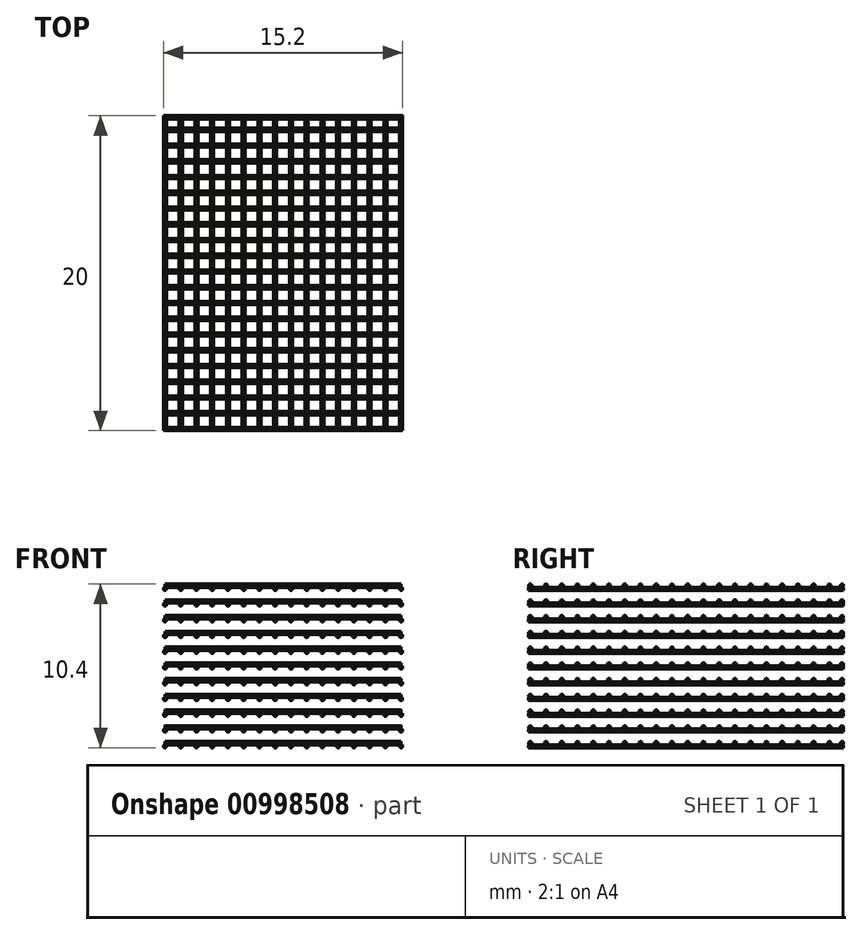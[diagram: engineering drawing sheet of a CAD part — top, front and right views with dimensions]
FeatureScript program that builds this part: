
annotation { "Feature Type Name" : "Feature", "Feature Type Description" : "" }
export const myFeature = defineFeature(function(context is Context, id is Id, definition is map)
    precondition{}
    {
        {
            var Q0;
            Q0=qCreatedBy(makeId("Front.planeOp"),FACE);
            var sketch = newSketch(context, id + "F0", { "sketchPlane" : qUnion([Q0])});
            skCircle(sketch, "E0", {"center": v(-15, 5) * mm, "radius": 0.1 * mm});
            skLineSegment(sketch, "E1.bottom", {"start": v(-15, 5) * mm, "end": v(0, 5) * mm, "construction": true});
            skLineSegment(sketch, "E1.top", {"start": v(-15, -5) * mm, "end": v(0, -5) * mm, "construction": true});
            skLineSegment(sketch, "E1.left", {"start": v(-15, 5) * mm, "end": v(-15, -5) * mm, "construction": true});
            skLineSegment(sketch, "E1.right", {"start": v(0, 5) * mm, "end": v(0, -5) * mm, "construction": true});
            skCircle(sketch, "E2", {"center": v(-15, -5) * mm, "radius": 0.1 * mm});
            skCircle(sketch, "E3", {"center": v(0, 5) * mm, "radius": 0.1 * mm});
            skCircle(sketch, "E4", {"center": v(0, -5) * mm, "radius": 0.1 * mm});
            skCircle(sketch, "E5", {"center": v(-15, 4) * mm, "radius": 0.1 * mm});
            skCircle(sketch, "E6", {"center": v(-15, 3) * mm, "radius": 0.1 * mm});
            skCircle(sketch, "E7", {"center": v(-15, 2) * mm, "radius": 0.1 * mm});
            skCircle(sketch, "E8", {"center": v(-15, 1) * mm, "radius": 0.1 * mm});
            skCircle(sketch, "E9", {"center": v(-15, 0) * mm, "radius": 0.1 * mm});
            skCircle(sketch, "E10", {"center": v(-15, -1) * mm, "radius": 0.1 * mm});
            skCircle(sketch, "E11", {"center": v(-15, -2) * mm, "radius": 0.1 * mm});
            skCircle(sketch, "E12", {"center": v(-15, -3) * mm, "radius": 0.1 * mm});
            skCircle(sketch, "E13", {"center": v(-15, -4) * mm, "radius": 0.1 * mm});
            skCircle(sketch, "E14", {"center": v(-10, 5) * mm, "radius": 0.1 * mm});
            skCircle(sketch, "E15", {"center": v(-9, 5) * mm, "radius": 0.1 * mm});
            skCircle(sketch, "E16", {"center": v(-8, 5) * mm, "radius": 0.1 * mm});
            skCircle(sketch, "E17", {"center": v(-7, 5) * mm, "radius": 0.1 * mm});
            skCircle(sketch, "E18", {"center": v(-6, 5) * mm, "radius": 0.1 * mm});
            skCircle(sketch, "E19", {"center": v(-5, 5) * mm, "radius": 0.1 * mm});
            skCircle(sketch, "E20", {"center": v(-4, 5) * mm, "radius": 0.1 * mm});
            skCircle(sketch, "E21", {"center": v(-3, 5) * mm, "radius": 0.1 * mm});
            skCircle(sketch, "E22", {"center": v(-2, 5) * mm, "radius": 0.1 * mm});
            skCircle(sketch, "E23", {"center": v(-1, 5) * mm, "radius": 0.1 * mm});
            skCircle(sketch, "E24", {"center": v(-13, 5) * mm, "radius": 0.1 * mm});
            skCircle(sketch, "E25", {"center": v(-12, 5) * mm, "radius": 0.1 * mm});
            skCircle(sketch, "E26", {"center": v(-11, 5) * mm, "radius": 0.1 * mm});
            skCircle(sketch, "E27", {"center": v(-14, 5) * mm, "radius": 0.1 * mm});
            skCircle(sketch, "E28", {"center": v(0, 4) * mm, "radius": 0.1 * mm});
            skCircle(sketch, "E29", {"center": v(0, 3) * mm, "radius": 0.1 * mm});
            skCircle(sketch, "E30", {"center": v(0, 2) * mm, "radius": 0.1 * mm});
            skCircle(sketch, "E31", {"center": v(0, -4) * mm, "radius": 0.1 * mm});
            skCircle(sketch, "E32", {"center": v(0, -3) * mm, "radius": 0.1 * mm});
            skCircle(sketch, "E33", {"center": v(0, 0) * mm, "radius": 0.1 * mm});
            skCircle(sketch, "E34", {"center": v(0, -2) * mm, "radius": 0.1 * mm});
            skCircle(sketch, "E35", {"center": v(0, -1) * mm, "radius": 0.1 * mm});
            skCircle(sketch, "E36", {"center": v(0, 1) * mm, "radius": 0.1 * mm});
            skCircle(sketch, "E37", {"center": v(-12, -5) * mm, "radius": 0.1 * mm});
            skCircle(sketch, "E38", {"center": v(-11, -5) * mm, "radius": 0.1 * mm});
            skCircle(sketch, "E39", {"center": v(-10, -5) * mm, "radius": 0.1 * mm});
            skCircle(sketch, "E40", {"center": v(-6, -5) * mm, "radius": 0.1 * mm});
            skCircle(sketch, "E41", {"center": v(-5, -5) * mm, "radius": 0.1 * mm});
            skCircle(sketch, "E42", {"center": v(-4, -5) * mm, "radius": 0.1 * mm});
            skCircle(sketch, "E43", {"center": v(-3, -5) * mm, "radius": 0.1 * mm});
            skCircle(sketch, "E44", {"center": v(-2, -5) * mm, "radius": 0.1 * mm});
            skCircle(sketch, "E45", {"center": v(-1, -5) * mm, "radius": 0.1 * mm});
            skCircle(sketch, "E46", {"center": v(-7, -5) * mm, "radius": 0.1 * mm});
            skCircle(sketch, "E47", {"center": v(-8, -5) * mm, "radius": 0.1 * mm});
            skCircle(sketch, "E48", {"center": v(-9, -5) * mm, "radius": 0.1 * mm});
            skCircle(sketch, "E49", {"center": v(-13, -5) * mm, "radius": 0.1 * mm});
            skCircle(sketch, "E50", {"center": v(-14, -5) * mm, "radius": 0.1 * mm});
            skLineSegment(sketch, "E51", {"start": v(-15, 4.5) * mm, "end": v(0, 4.5) * mm, "construction": true});
            skLineSegment(sketch, "E52", {"start": v(-15, 3.5) * mm, "end": v(0, 3.5) * mm, "construction": true});
            skLineSegment(sketch, "E53", {"start": v(-15, 2.5) * mm, "end": v(0, 2.5) * mm, "construction": true});
            skLineSegment(sketch, "E54", {"start": v(-15, 1.5) * mm, "end": v(0, 1.5) * mm, "construction": true});
            skCircle(sketch, "E55.MirrorC", {"center": v(-14, 4) * mm, "radius": 0.1 * mm});
            skLineSegment(sketch, "E56", {"start": v(-15, 0.5) * mm, "end": v(0, 0.5) * mm, "construction": true});
            skCircle(sketch, "E57.MirrorC", {"center": v(-13, 4) * mm, "radius": 0.1 * mm});
            skCircle(sketch, "E58.MirrorC", {"center": v(-12, 4) * mm, "radius": 0.1 * mm});
            skCircle(sketch, "E59.MirrorC", {"center": v(-11, 4) * mm, "radius": 0.1 * mm});
            skCircle(sketch, "E60.MirrorC", {"center": v(-10, 4) * mm, "radius": 0.1 * mm});
            skCircle(sketch, "E61.MirrorC", {"center": v(-9, 4) * mm, "radius": 0.1 * mm});
            skCircle(sketch, "E62.MirrorC", {"center": v(-8, 4) * mm, "radius": 0.1 * mm});
            skCircle(sketch, "E63.MirrorC", {"center": v(-7, 4) * mm, "radius": 0.1 * mm});
            skCircle(sketch, "E64.MirrorC", {"center": v(-6, 4) * mm, "radius": 0.1 * mm});
            skCircle(sketch, "E65.MirrorC", {"center": v(-5, 4) * mm, "radius": 0.1 * mm});
            skCircle(sketch, "E66.MirrorC", {"center": v(-4, 4) * mm, "radius": 0.1 * mm});
            skCircle(sketch, "E67.MirrorC", {"center": v(-3, 4) * mm, "radius": 0.1 * mm});
            skCircle(sketch, "E68.MirrorC", {"center": v(-2, 4) * mm, "radius": 0.1 * mm});
            skCircle(sketch, "E69.MirrorC", {"center": v(-1, 4) * mm, "radius": 0.1 * mm});
            skCircle(sketch, "E70.MirrorC", {"center": v(-1, 3) * mm, "radius": 0.1 * mm});
            skCircle(sketch, "E71.MirrorC", {"center": v(-2, 3) * mm, "radius": 0.1 * mm});
            skCircle(sketch, "E72.MirrorC", {"center": v(-3, 3) * mm, "radius": 0.1 * mm});
            skCircle(sketch, "E73.MirrorC", {"center": v(-4, 3) * mm, "radius": 0.1 * mm});
            skCircle(sketch, "E74.MirrorC", {"center": v(-5, 3) * mm, "radius": 0.1 * mm});
            skCircle(sketch, "E75.MirrorC", {"center": v(-6, 3) * mm, "radius": 0.1 * mm});
            skCircle(sketch, "E76.MirrorC", {"center": v(-7, 3) * mm, "radius": 0.1 * mm});
            skCircle(sketch, "E77.MirrorC", {"center": v(-8, 3) * mm, "radius": 0.1 * mm});
            skCircle(sketch, "E78.MirrorC", {"center": v(-9, 3) * mm, "radius": 0.1 * mm});
            skCircle(sketch, "E79.MirrorC", {"center": v(-10, 3) * mm, "radius": 0.1 * mm});
            skCircle(sketch, "E80.MirrorC", {"center": v(-11, 3) * mm, "radius": 0.1 * mm});
            skCircle(sketch, "E81.MirrorC", {"center": v(-12, 3) * mm, "radius": 0.1 * mm});
            skCircle(sketch, "E82.MirrorC", {"center": v(-13, 3) * mm, "radius": 0.1 * mm});
            skCircle(sketch, "E83.MirrorC", {"center": v(-14, 3) * mm, "radius": 0.1 * mm});
            skCircle(sketch, "E84.MirrorC", {"center": v(-14, 2) * mm, "radius": 0.1 * mm});
            skCircle(sketch, "E85.MirrorC", {"center": v(-13, 2) * mm, "radius": 0.1 * mm});
            skCircle(sketch, "E86.MirrorC", {"center": v(-12, 2) * mm, "radius": 0.1 * mm});
            skCircle(sketch, "E87.MirrorC", {"center": v(-11, 2) * mm, "radius": 0.1 * mm});
            skCircle(sketch, "E88.MirrorC", {"center": v(-10, 2) * mm, "radius": 0.1 * mm});
            skCircle(sketch, "E89.MirrorC", {"center": v(-9, 2) * mm, "radius": 0.1 * mm});
            skCircle(sketch, "E90.MirrorC", {"center": v(-8, 2) * mm, "radius": 0.1 * mm});
            skCircle(sketch, "E91.MirrorC", {"center": v(-7, 2) * mm, "radius": 0.1 * mm});
            skCircle(sketch, "E92.MirrorC", {"center": v(-6, 2) * mm, "radius": 0.1 * mm});
            skCircle(sketch, "E93.MirrorC", {"center": v(-5, 2) * mm, "radius": 0.1 * mm});
            skCircle(sketch, "E94.MirrorC", {"center": v(-4, 2) * mm, "radius": 0.1 * mm});
            skCircle(sketch, "E95.MirrorC", {"center": v(-3, 2) * mm, "radius": 0.1 * mm});
            skCircle(sketch, "E96.MirrorC", {"center": v(-2, 2) * mm, "radius": 0.1 * mm});
            skCircle(sketch, "E97.MirrorC", {"center": v(-1, 2) * mm, "radius": 0.1 * mm});
            skCircle(sketch, "E98.MirrorC", {"center": v(-1, 1) * mm, "radius": 0.1 * mm});
            skCircle(sketch, "E99.MirrorC", {"center": v(-2, 1) * mm, "radius": 0.1 * mm});
            skCircle(sketch, "E100.MirrorC", {"center": v(-3, 1) * mm, "radius": 0.1 * mm});
            skCircle(sketch, "E101.MirrorC", {"center": v(-4, 1) * mm, "radius": 0.1 * mm});
            skCircle(sketch, "E102.MirrorC", {"center": v(-5, 1) * mm, "radius": 0.1 * mm});
            skCircle(sketch, "E103.MirrorC", {"center": v(-6, 1) * mm, "radius": 0.1 * mm});
            skCircle(sketch, "E104.MirrorC", {"center": v(-7, 1) * mm, "radius": 0.1 * mm});
            skCircle(sketch, "E105.MirrorC", {"center": v(-8, 1) * mm, "radius": 0.1 * mm});
            skCircle(sketch, "E106.MirrorC", {"center": v(-9, 1) * mm, "radius": 0.1 * mm});
            skCircle(sketch, "E107.MirrorC", {"center": v(-10, 1) * mm, "radius": 0.1 * mm});
            skCircle(sketch, "E108.MirrorC", {"center": v(-11, 1) * mm, "radius": 0.1 * mm});
            skCircle(sketch, "E109.MirrorC", {"center": v(-12, 1) * mm, "radius": 0.1 * mm});
            skCircle(sketch, "E110.MirrorC", {"center": v(-13, 1) * mm, "radius": 0.1 * mm});
            skCircle(sketch, "E111.MirrorC", {"center": v(-14, 1) * mm, "radius": 0.1 * mm});
            skCircle(sketch, "E112.MirrorC", {"center": v(-14, 0) * mm, "radius": 0.1 * mm});
            skCircle(sketch, "E113.MirrorC", {"center": v(-13, 0) * mm, "radius": 0.1 * mm});
            skCircle(sketch, "E114.MirrorC", {"center": v(-12, 0) * mm, "radius": 0.1 * mm});
            skCircle(sketch, "E115.MirrorC", {"center": v(-11, 0) * mm, "radius": 0.1 * mm});
            skCircle(sketch, "E116.MirrorC", {"center": v(-10, 0) * mm, "radius": 0.1 * mm});
            skCircle(sketch, "E117.MirrorC", {"center": v(-9, 0) * mm, "radius": 0.1 * mm});
            skCircle(sketch, "E118.MirrorC", {"center": v(-8, 0) * mm, "radius": 0.1 * mm});
            skCircle(sketch, "E119.MirrorC", {"center": v(-7, 0) * mm, "radius": 0.1 * mm});
            skCircle(sketch, "E120.MirrorC", {"center": v(-6, 0) * mm, "radius": 0.1 * mm});
            skCircle(sketch, "E121.MirrorC", {"center": v(-5, 0) * mm, "radius": 0.1 * mm});
            skCircle(sketch, "E122.MirrorC", {"center": v(-4, 0) * mm, "radius": 0.1 * mm});
            skCircle(sketch, "E123.MirrorC", {"center": v(-3, 0) * mm, "radius": 0.1 * mm});
            skCircle(sketch, "E124.MirrorC", {"center": v(-2, 0) * mm, "radius": 0.1 * mm});
            skCircle(sketch, "E125.MirrorC", {"center": v(-1, 0) * mm, "radius": 0.1 * mm});
            skCircle(sketch, "E126.MirrorC", {"center": v(-13, -4) * mm, "radius": 0.1 * mm});
            skCircle(sketch, "E127.MirrorC", {"center": v(-2, -4) * mm, "radius": 0.1 * mm});
            skCircle(sketch, "E128.MirrorC", {"center": v(-1, -4) * mm, "radius": 0.1 * mm});
            skCircle(sketch, "E129.MirrorC", {"center": v(-8, -4) * mm, "radius": 0.1 * mm});
            skCircle(sketch, "E130.MirrorC", {"center": v(-3, -4) * mm, "radius": 0.1 * mm});
            skCircle(sketch, "E131.MirrorC", {"center": v(-14, -4) * mm, "radius": 0.1 * mm});
            skCircle(sketch, "E132.MirrorC", {"center": v(-12, -4) * mm, "radius": 0.1 * mm});
            skCircle(sketch, "E133.MirrorC", {"center": v(-9, -4) * mm, "radius": 0.1 * mm});
            skCircle(sketch, "E134.MirrorC", {"center": v(-6, -4) * mm, "radius": 0.1 * mm});
            skCircle(sketch, "E135.MirrorC", {"center": v(-7, -4) * mm, "radius": 0.1 * mm});
            skCircle(sketch, "E136.MirrorC", {"center": v(-5, -4) * mm, "radius": 0.1 * mm});
            skCircle(sketch, "E137.MirrorC", {"center": v(-11, -4) * mm, "radius": 0.1 * mm});
            skCircle(sketch, "E138.MirrorC", {"center": v(-10, -4) * mm, "radius": 0.1 * mm});
            skCircle(sketch, "E139.MirrorC", {"center": v(-4, -4) * mm, "radius": 0.1 * mm});
            skCircle(sketch, "E140.MirrorC", {"center": v(-2, -3) * mm, "radius": 0.1 * mm});
            skCircle(sketch, "E141.MirrorC", {"center": v(-1, -3) * mm, "radius": 0.1 * mm});
            skCircle(sketch, "E142.MirrorC", {"center": v(-7, -3) * mm, "radius": 0.1 * mm});
            skCircle(sketch, "E143.MirrorC", {"center": v(-3, -3) * mm, "radius": 0.1 * mm});
            skCircle(sketch, "E144.MirrorC", {"center": v(-4, -3) * mm, "radius": 0.1 * mm});
            skCircle(sketch, "E145.MirrorC", {"center": v(-9, -3) * mm, "radius": 0.1 * mm});
            skCircle(sketch, "E146.MirrorC", {"center": v(-8, -3) * mm, "radius": 0.1 * mm});
            skCircle(sketch, "E147.MirrorC", {"center": v(-12, -3) * mm, "radius": 0.1 * mm});
            skCircle(sketch, "E148.MirrorC", {"center": v(-5, -3) * mm, "radius": 0.1 * mm});
            skCircle(sketch, "E149.MirrorC", {"center": v(-10, -3) * mm, "radius": 0.1 * mm});
            skCircle(sketch, "E150.MirrorC", {"center": v(-6, -3) * mm, "radius": 0.1 * mm});
            skCircle(sketch, "E151.MirrorC", {"center": v(-11, -3) * mm, "radius": 0.1 * mm});
            skCircle(sketch, "E152.MirrorC", {"center": v(-14, -3) * mm, "radius": 0.1 * mm});
            skCircle(sketch, "E153.MirrorC", {"center": v(-13, -3) * mm, "radius": 0.1 * mm});
            skCircle(sketch, "E154.MirrorC", {"center": v(-9, -2) * mm, "radius": 0.1 * mm});
            skCircle(sketch, "E155.MirrorC", {"center": v(-2, -2) * mm, "radius": 0.1 * mm});
            skCircle(sketch, "E156.MirrorC", {"center": v(-12, -2) * mm, "radius": 0.1 * mm});
            skCircle(sketch, "E157.MirrorC", {"center": v(-3, -2) * mm, "radius": 0.1 * mm});
            skCircle(sketch, "E158.MirrorC", {"center": v(-7, -2) * mm, "radius": 0.1 * mm});
            skCircle(sketch, "E159.MirrorC", {"center": v(-14, -2) * mm, "radius": 0.1 * mm});
            skCircle(sketch, "E160.MirrorC", {"center": v(-1, -2) * mm, "radius": 0.1 * mm});
            skCircle(sketch, "E161.MirrorC", {"center": v(-8, -2) * mm, "radius": 0.1 * mm});
            skCircle(sketch, "E162.MirrorC", {"center": v(-6, -2) * mm, "radius": 0.1 * mm});
            skCircle(sketch, "E163.MirrorC", {"center": v(-10, -2) * mm, "radius": 0.1 * mm});
            skCircle(sketch, "E164.MirrorC", {"center": v(-13, -2) * mm, "radius": 0.1 * mm});
            skCircle(sketch, "E165.MirrorC", {"center": v(-5, -2) * mm, "radius": 0.1 * mm});
            skCircle(sketch, "E166.MirrorC", {"center": v(-11, -2) * mm, "radius": 0.1 * mm});
            skCircle(sketch, "E167.MirrorC", {"center": v(-4, -2) * mm, "radius": 0.1 * mm});
            skCircle(sketch, "E168.MirrorC", {"center": v(-6, -1) * mm, "radius": 0.1 * mm});
            skCircle(sketch, "E169.MirrorC", {"center": v(-9, -1) * mm, "radius": 0.1 * mm});
            skCircle(sketch, "E170.MirrorC", {"center": v(-7, -1) * mm, "radius": 0.1 * mm});
            skCircle(sketch, "E171.MirrorC", {"center": v(-3, -1) * mm, "radius": 0.1 * mm});
            skCircle(sketch, "E172.MirrorC", {"center": v(-5, -1) * mm, "radius": 0.1 * mm});
            skCircle(sketch, "E173.MirrorC", {"center": v(-1, -1) * mm, "radius": 0.1 * mm});
            skCircle(sketch, "E174.MirrorC", {"center": v(-13, -1) * mm, "radius": 0.1 * mm});
            skCircle(sketch, "E175.MirrorC", {"center": v(-12, -1) * mm, "radius": 0.1 * mm});
            skCircle(sketch, "E176.MirrorC", {"center": v(-8, -1) * mm, "radius": 0.1 * mm});
            skCircle(sketch, "E177.MirrorC", {"center": v(-2, -1) * mm, "radius": 0.1 * mm});
            skCircle(sketch, "E178.MirrorC", {"center": v(-10, -1) * mm, "radius": 0.1 * mm});
            skCircle(sketch, "E179.MirrorC", {"center": v(-11, -1) * mm, "radius": 0.1 * mm});
            skCircle(sketch, "E180.MirrorC", {"center": v(-4, -1) * mm, "radius": 0.1 * mm});
            skCircle(sketch, "E181.MirrorC", {"center": v(-14, -1) * mm, "radius": 0.1 * mm});
            skSolve(sketch);
        }
        {
            var Q0;
            Q0 = qSketchRegion(id + "F0", true);
            extrude(context, id + "F1", {"entities" : qUnion([Q0]), "depth" : 20 * mm, "offsetDistance" : 25 * mm});
        }
        {
            var Q0;
            Q0=qCreatedBy(makeId("Right.planeOp"),FACE);
            var sketch = newSketch(context, id + "F2", { "sketchPlane" : qUnion([Q0])});
            skLineSegment(sketch, "E182.bottom", {"start": v(-20, 5) * mm, "end": v(0, 5) * mm, "construction": true});
            skLineSegment(sketch, "E182.top", {"start": v(-20, -5) * mm, "end": v(0, -5) * mm, "construction": true});
            skLineSegment(sketch, "E182.left", {"start": v(-20, 5) * mm, "end": v(-20, -5) * mm, "construction": true});
            skLineSegment(sketch, "E182.right", {"start": v(0, 5) * mm, "end": v(0, -5) * mm, "construction": true});
            skCircle(sketch, "E183", {"center": v(-19.9, 4.2) * mm, "radius": 0.1 * mm});
            skCircle(sketch, "E184", {"center": v(-19.9, 3.2) * mm, "radius": 0.1 * mm});
            skCircle(sketch, "E185", {"center": v(-19.9, 2.2) * mm, "radius": 0.1 * mm});
            skCircle(sketch, "E186", {"center": v(-19.9, 1.2) * mm, "radius": 0.1 * mm});
            skCircle(sketch, "E187", {"center": v(-19.9, 0.2) * mm, "radius": 0.1 * mm});
            skCircle(sketch, "E188", {"center": v(-19.9, -0.8) * mm, "radius": 0.1 * mm});
            skCircle(sketch, "E189", {"center": v(-19.9, -1.8) * mm, "radius": 0.1 * mm});
            skCircle(sketch, "E190", {"center": v(-19.9, -2.8) * mm, "radius": 0.1 * mm});
            skCircle(sketch, "E191", {"center": v(-19.9, -3.8) * mm, "radius": 0.1 * mm});
            skCircle(sketch, "E192", {"center": v(-19.9, -4.8) * mm, "radius": 0.1 * mm});
            skCircle(sketch, "E193", {"center": v(-19.9, 5.2) * mm, "radius": 0.1 * mm});
            skCircle(sketch, "E194", {"center": v(-18.9, -4.8) * mm, "radius": 0.1 * mm});
            skCircle(sketch, "E195", {"center": v(-17.9, -4.8) * mm, "radius": 0.1 * mm});
            skCircle(sketch, "E196", {"center": v(-12.9, -4.8) * mm, "radius": 0.1 * mm});
            skCircle(sketch, "E197", {"center": v(-16.9, -4.8) * mm, "radius": 0.1 * mm});
            skCircle(sketch, "E198", {"center": v(-11.9, -4.8) * mm, "radius": 0.1 * mm});
            skCircle(sketch, "E199", {"center": v(-10.9, -4.8) * mm, "radius": 0.1 * mm});
            skCircle(sketch, "E200", {"center": v(-15.9, -4.8) * mm, "radius": 0.1 * mm});
            skCircle(sketch, "E201", {"center": v(-9.9, -4.8) * mm, "radius": 0.1 * mm});
            skCircle(sketch, "E202", {"center": v(-8.9, -4.8) * mm, "radius": 0.1 * mm});
            skCircle(sketch, "E203", {"center": v(-14.9, -4.8) * mm, "radius": 0.1 * mm});
            skCircle(sketch, "E204", {"center": v(-13.9, -4.8) * mm, "radius": 0.1 * mm});
            skCircle(sketch, "E205", {"center": v(-7.9, -4.8) * mm, "radius": 0.1 * mm});
            skCircle(sketch, "E206", {"center": v(-6.9, -4.8) * mm, "radius": 0.1 * mm});
            skCircle(sketch, "E207", {"center": v(-5.9, -4.8) * mm, "radius": 0.1 * mm});
            skCircle(sketch, "E208", {"center": v(-4.9, -4.8) * mm, "radius": 0.1 * mm});
            skCircle(sketch, "E209", {"center": v(-3.9, -4.8) * mm, "radius": 0.1 * mm});
            skCircle(sketch, "E210", {"center": v(-2.9, -4.8) * mm, "radius": 0.1 * mm});
            skCircle(sketch, "E211", {"center": v(-1.9, -4.8) * mm, "radius": 0.1 * mm});
            skCircle(sketch, "E212", {"center": v(-0.9, -4.8) * mm, "radius": 0.1 * mm});
            skCircle(sketch, "E213", {"center": v(-0.1, -4.8) * mm, "radius": 0.1 * mm});
            skCircle(sketch, "E214", {"center": v(-0.1, -3.8) * mm, "radius": 0.1 * mm});
            skCircle(sketch, "E215", {"center": v(-0.1, -2.8) * mm, "radius": 0.1 * mm});
            skCircle(sketch, "E216", {"center": v(-0.1, -1.8) * mm, "radius": 0.1 * mm});
            skCircle(sketch, "E217", {"center": v(-0.1, -0.8) * mm, "radius": 0.1 * mm});
            skCircle(sketch, "E218", {"center": v(-0.1, 0.2) * mm, "radius": 0.1 * mm});
            skCircle(sketch, "E219", {"center": v(-0.1, 1.2) * mm, "radius": 0.1 * mm});
            skCircle(sketch, "E220", {"center": v(-0.1, 2.2) * mm, "radius": 0.1 * mm});
            skCircle(sketch, "E221", {"center": v(-0.1, 3.2) * mm, "radius": 0.1 * mm});
            skCircle(sketch, "E222", {"center": v(-0.1, 4.2) * mm, "radius": 0.1 * mm});
            skCircle(sketch, "E223", {"center": v(-0.1, 5.2) * mm, "radius": 0.1 * mm});
            skCircle(sketch, "E224", {"center": v(-18.9, 5.2) * mm, "radius": 0.1 * mm});
            skCircle(sketch, "E225", {"center": v(-17.9, 5.2) * mm, "radius": 0.1 * mm});
            skCircle(sketch, "E226", {"center": v(-16.9, 5.2) * mm, "radius": 0.1 * mm});
            skCircle(sketch, "E227", {"center": v(-15.9, 5.2) * mm, "radius": 0.1 * mm});
            skCircle(sketch, "E228", {"center": v(-14.9, 5.2) * mm, "radius": 0.1 * mm});
            skCircle(sketch, "E229", {"center": v(-13.9, 5.2) * mm, "radius": 0.1 * mm});
            skCircle(sketch, "E230", {"center": v(-12.9, 5.2) * mm, "radius": 0.1 * mm});
            skCircle(sketch, "E231", {"center": v(-11.9, 5.2) * mm, "radius": 0.1 * mm});
            skCircle(sketch, "E232", {"center": v(-10.9, 5.2) * mm, "radius": 0.1 * mm});
            skCircle(sketch, "E233", {"center": v(-9.9, 5.2) * mm, "radius": 0.1 * mm});
            skCircle(sketch, "E234", {"center": v(-8.9, 5.2) * mm, "radius": 0.1 * mm});
            skCircle(sketch, "E235", {"center": v(-7.9, 5.2) * mm, "radius": 0.1 * mm});
            skCircle(sketch, "E236", {"center": v(-6.9, 5.2) * mm, "radius": 0.1 * mm});
            skCircle(sketch, "E237", {"center": v(-5.9, 5.2) * mm, "radius": 0.1 * mm});
            skCircle(sketch, "E238", {"center": v(-4.9, 5.2) * mm, "radius": 0.1 * mm});
            skCircle(sketch, "E239", {"center": v(-3.9, 5.2) * mm, "radius": 0.1 * mm});
            skCircle(sketch, "E240", {"center": v(-2.9, 5.2) * mm, "radius": 0.1 * mm});
            skCircle(sketch, "E241", {"center": v(-1.9, 5.2) * mm, "radius": 0.1 * mm});
            skCircle(sketch, "E242", {"center": v(-0.9, 5.2) * mm, "radius": 0.1 * mm});
            skLineSegment(sketch, "E243", {"start": v(-20, 4.7) * mm, "end": v(0, 4.7) * mm, "construction": true});
            skLineSegment(sketch, "E244", {"start": v(-20, 3.7) * mm, "end": v(0, 3.7) * mm, "construction": true});
            skLineSegment(sketch, "E245", {"start": v(-20, 2.7) * mm, "end": v(0, 2.7) * mm, "construction": true});
            skLineSegment(sketch, "E246", {"start": v(-20, 1.7) * mm, "end": v(0, 1.7) * mm, "construction": true});
            skLineSegment(sketch, "E247", {"start": v(-20, 0.7) * mm, "end": v(0, 0.7) * mm, "construction": true});
            skCircle(sketch, "E248.MirrorC", {"center": v(-0.9, 4.2) * mm, "radius": 0.1 * mm});
            skCircle(sketch, "E249.MirrorC", {"center": v(-6.9, 4.2) * mm, "radius": 0.1 * mm});
            skCircle(sketch, "E250.MirrorC", {"center": v(-4.9, 4.2) * mm, "radius": 0.1 * mm});
            skCircle(sketch, "E251.MirrorC", {"center": v(-5.9, 4.2) * mm, "radius": 0.1 * mm});
            skCircle(sketch, "E252.MirrorC", {"center": v(-3.9, 4.2) * mm, "radius": 0.1 * mm});
            skCircle(sketch, "E253.MirrorC", {"center": v(-2.9, 4.2) * mm, "radius": 0.1 * mm});
            skCircle(sketch, "E254.MirrorC", {"center": v(-8.9, 4.2) * mm, "radius": 0.1 * mm});
            skCircle(sketch, "E255.MirrorC", {"center": v(-1.9, 4.2) * mm, "radius": 0.1 * mm});
            skCircle(sketch, "E256.MirrorC", {"center": v(-7.9, 4.2) * mm, "radius": 0.1 * mm});
            skCircle(sketch, "E257.MirrorC", {"center": v(-11.9, 4.2) * mm, "radius": 0.1 * mm});
            skCircle(sketch, "E258.MirrorC", {"center": v(-14.9, 4.2) * mm, "radius": 0.1 * mm});
            skCircle(sketch, "E259.MirrorC", {"center": v(-10.9, 4.2) * mm, "radius": 0.1 * mm});
            skCircle(sketch, "E260.MirrorC", {"center": v(-15.9, 4.2) * mm, "radius": 0.1 * mm});
            skCircle(sketch, "E261.MirrorC", {"center": v(-9.9, 4.2) * mm, "radius": 0.1 * mm});
            skCircle(sketch, "E262.MirrorC", {"center": v(-18.9, 4.2) * mm, "radius": 0.1 * mm});
            skCircle(sketch, "E263.MirrorC", {"center": v(-13.9, 4.2) * mm, "radius": 0.1 * mm});
            skCircle(sketch, "E264.MirrorC", {"center": v(-12.9, 4.2) * mm, "radius": 0.1 * mm});
            skCircle(sketch, "E265.MirrorC", {"center": v(-17.9, 4.2) * mm, "radius": 0.1 * mm});
            skCircle(sketch, "E266.MirrorC", {"center": v(-16.9, 4.2) * mm, "radius": 0.1 * mm});
            skCircle(sketch, "E267.MirrorC", {"center": v(-17.9, 3.2) * mm, "radius": 0.1 * mm});
            skCircle(sketch, "E268.MirrorC", {"center": v(-4.9, 3.2) * mm, "radius": 0.1 * mm});
            skCircle(sketch, "E269.MirrorC", {"center": v(-5.9, 3.2) * mm, "radius": 0.1 * mm});
            skCircle(sketch, "E270.MirrorC", {"center": v(-9.9, 3.2) * mm, "radius": 0.1 * mm});
            skCircle(sketch, "E271.MirrorC", {"center": v(-8.9, 3.2) * mm, "radius": 0.1 * mm});
            skCircle(sketch, "E272.MirrorC", {"center": v(-2.9, 3.2) * mm, "radius": 0.1 * mm});
            skCircle(sketch, "E273.MirrorC", {"center": v(-13.9, 3.2) * mm, "radius": 0.1 * mm});
            skCircle(sketch, "E274.MirrorC", {"center": v(-0.9, 3.2) * mm, "radius": 0.1 * mm});
            skCircle(sketch, "E275.MirrorC", {"center": v(-3.9, 3.2) * mm, "radius": 0.1 * mm});
            skCircle(sketch, "E276.MirrorC", {"center": v(-10.9, 3.2) * mm, "radius": 0.1 * mm});
            skCircle(sketch, "E277.MirrorC", {"center": v(-18.9, 3.2) * mm, "radius": 0.1 * mm});
            skCircle(sketch, "E278.MirrorC", {"center": v(-6.9, 3.2) * mm, "radius": 0.1 * mm});
            skCircle(sketch, "E279.MirrorC", {"center": v(-15.9, 3.2) * mm, "radius": 0.1 * mm});
            skCircle(sketch, "E280.MirrorC", {"center": v(-14.9, 3.2) * mm, "radius": 0.1 * mm});
            skCircle(sketch, "E281.MirrorC", {"center": v(-12.9, 3.2) * mm, "radius": 0.1 * mm});
            skCircle(sketch, "E282.MirrorC", {"center": v(-1.9, 3.2) * mm, "radius": 0.1 * mm});
            skCircle(sketch, "E283.MirrorC", {"center": v(-16.9, 3.2) * mm, "radius": 0.1 * mm});
            skCircle(sketch, "E284.MirrorC", {"center": v(-11.9, 3.2) * mm, "radius": 0.1 * mm});
            skCircle(sketch, "E285.MirrorC", {"center": v(-7.9, 3.2) * mm, "radius": 0.1 * mm});
            skCircle(sketch, "E286.MirrorC", {"center": v(-17.9, 2.2) * mm, "radius": 0.1 * mm});
            skCircle(sketch, "E287.MirrorC", {"center": v(-4.9, 2.2) * mm, "radius": 0.1 * mm});
            skCircle(sketch, "E288.MirrorC", {"center": v(-3.9, 2.2) * mm, "radius": 0.1 * mm});
            skCircle(sketch, "E289.MirrorC", {"center": v(-11.9, 2.2) * mm, "radius": 0.1 * mm});
            skCircle(sketch, "E290.MirrorC", {"center": v(-14.9, 2.2) * mm, "radius": 0.1 * mm});
            skCircle(sketch, "E291.MirrorC", {"center": v(-5.9, 2.2) * mm, "radius": 0.1 * mm});
            skCircle(sketch, "E292.MirrorC", {"center": v(-2.9, 2.2) * mm, "radius": 0.1 * mm});
            skCircle(sketch, "E293.MirrorC", {"center": v(-0.9, 2.2) * mm, "radius": 0.1 * mm});
            skCircle(sketch, "E294.MirrorC", {"center": v(-8.9, 2.2) * mm, "radius": 0.1 * mm});
            skCircle(sketch, "E295.MirrorC", {"center": v(-9.9, 2.2) * mm, "radius": 0.1 * mm});
            skCircle(sketch, "E296.MirrorC", {"center": v(-16.9, 2.2) * mm, "radius": 0.1 * mm});
            skCircle(sketch, "E297.MirrorC", {"center": v(-12.9, 2.2) * mm, "radius": 0.1 * mm});
            skCircle(sketch, "E298.MirrorC", {"center": v(-7.9, 2.2) * mm, "radius": 0.1 * mm});
            skCircle(sketch, "E299.MirrorC", {"center": v(-15.9, 2.2) * mm, "radius": 0.1 * mm});
            skCircle(sketch, "E300.MirrorC", {"center": v(-1.9, 2.2) * mm, "radius": 0.1 * mm});
            skCircle(sketch, "E301.MirrorC", {"center": v(-6.9, 2.2) * mm, "radius": 0.1 * mm});
            skCircle(sketch, "E302.MirrorC", {"center": v(-18.9, 2.2) * mm, "radius": 0.1 * mm});
            skCircle(sketch, "E303.MirrorC", {"center": v(-13.9, 2.2) * mm, "radius": 0.1 * mm});
            skCircle(sketch, "E304.MirrorC", {"center": v(-10.9, 2.2) * mm, "radius": 0.1 * mm});
            skCircle(sketch, "E305.MirrorC", {"center": v(-2.9, 1.2) * mm, "radius": 0.1 * mm});
            skCircle(sketch, "E306.MirrorC", {"center": v(-12.9, 1.2) * mm, "radius": 0.1 * mm});
            skCircle(sketch, "E307.MirrorC", {"center": v(-1.9, 1.2) * mm, "radius": 0.1 * mm});
            skCircle(sketch, "E308.MirrorC", {"center": v(-4.9, 1.2) * mm, "radius": 0.1 * mm});
            skCircle(sketch, "E309.MirrorC", {"center": v(-13.9, 1.2) * mm, "radius": 0.1 * mm});
            skCircle(sketch, "E310.MirrorC", {"center": v(-14.9, 1.2) * mm, "radius": 0.1 * mm});
            skCircle(sketch, "E311.MirrorC", {"center": v(-10.9, 1.2) * mm, "radius": 0.1 * mm});
            skCircle(sketch, "E312.MirrorC", {"center": v(-16.9, 1.2) * mm, "radius": 0.1 * mm});
            skCircle(sketch, "E313.MirrorC", {"center": v(-11.9, 1.2) * mm, "radius": 0.1 * mm});
            skCircle(sketch, "E314.MirrorC", {"center": v(-5.9, 1.2) * mm, "radius": 0.1 * mm});
            skCircle(sketch, "E315.MirrorC", {"center": v(-8.9, 1.2) * mm, "radius": 0.1 * mm});
            skCircle(sketch, "E316.MirrorC", {"center": v(-0.9, 1.2) * mm, "radius": 0.1 * mm});
            skCircle(sketch, "E317.MirrorC", {"center": v(-15.9, 1.2) * mm, "radius": 0.1 * mm});
            skCircle(sketch, "E318.MirrorC", {"center": v(-9.9, 1.2) * mm, "radius": 0.1 * mm});
            skCircle(sketch, "E319.MirrorC", {"center": v(-18.9, 1.2) * mm, "radius": 0.1 * mm});
            skCircle(sketch, "E320.MirrorC", {"center": v(-17.9, 1.2) * mm, "radius": 0.1 * mm});
            skCircle(sketch, "E321.MirrorC", {"center": v(-7.9, 1.2) * mm, "radius": 0.1 * mm});
            skCircle(sketch, "E322.MirrorC", {"center": v(-3.9, 1.2) * mm, "radius": 0.1 * mm});
            skCircle(sketch, "E323.MirrorC", {"center": v(-6.9, 1.2) * mm, "radius": 0.1 * mm});
            skCircle(sketch, "E324.MirrorC", {"center": v(-13.9, 0.2) * mm, "radius": 0.1 * mm});
            skCircle(sketch, "E325.MirrorC", {"center": v(-1.9, 0.2) * mm, "radius": 0.1 * mm});
            skCircle(sketch, "E326.MirrorC", {"center": v(-18.9, 0.2) * mm, "radius": 0.1 * mm});
            skCircle(sketch, "E327.MirrorC", {"center": v(-4.9, 0.2) * mm, "radius": 0.1 * mm});
            skCircle(sketch, "E328.MirrorC", {"center": v(-10.9, 0.2) * mm, "radius": 0.1 * mm});
            skCircle(sketch, "E329.MirrorC", {"center": v(-14.9, 0.2) * mm, "radius": 0.1 * mm});
            skCircle(sketch, "E330.MirrorC", {"center": v(-15.9, 0.2) * mm, "radius": 0.1 * mm});
            skCircle(sketch, "E331.MirrorC", {"center": v(-2.9, 0.2) * mm, "radius": 0.1 * mm});
            skCircle(sketch, "E332.MirrorC", {"center": v(-8.9, 0.2) * mm, "radius": 0.1 * mm});
            skCircle(sketch, "E333.MirrorC", {"center": v(-5.9, 0.2) * mm, "radius": 0.1 * mm});
            skCircle(sketch, "E334.MirrorC", {"center": v(-11.9, 0.2) * mm, "radius": 0.1 * mm});
            skCircle(sketch, "E335.MirrorC", {"center": v(-17.9, 0.2) * mm, "radius": 0.1 * mm});
            skCircle(sketch, "E336.MirrorC", {"center": v(-3.9, 0.2) * mm, "radius": 0.1 * mm});
            skCircle(sketch, "E337.MirrorC", {"center": v(-7.9, 0.2) * mm, "radius": 0.1 * mm});
            skCircle(sketch, "E338.MirrorC", {"center": v(-9.9, 0.2) * mm, "radius": 0.1 * mm});
            skCircle(sketch, "E339.MirrorC", {"center": v(-12.9, 0.2) * mm, "radius": 0.1 * mm});
            skCircle(sketch, "E340.MirrorC", {"center": v(-6.9, 0.2) * mm, "radius": 0.1 * mm});
            skCircle(sketch, "E341.MirrorC", {"center": v(-16.9, 0.2) * mm, "radius": 0.1 * mm});
            skCircle(sketch, "E342.MirrorC", {"center": v(-0.9, 0.2) * mm, "radius": 0.1 * mm});
            skLineSegment(sketch, "E343", {"start": v(0, -4.3) * mm, "end": v(-20, -4.3) * mm, "construction": true});
            skLineSegment(sketch, "E344", {"start": v(-20, -3.3) * mm, "end": v(0, -3.3) * mm, "construction": true});
            skLineSegment(sketch, "E345", {"start": v(-20, -2.3) * mm, "end": v(0, -2.3) * mm, "construction": true});
            skLineSegment(sketch, "E346", {"start": v(-20, -1.3) * mm, "end": v(0, -1.3) * mm, "construction": true});
            skCircle(sketch, "E347.MirrorC", {"center": v(-1.9, -3.8) * mm, "radius": 0.1 * mm});
            skCircle(sketch, "E348.MirrorC", {"center": v(-6.9, -3.8) * mm, "radius": 0.1 * mm});
            skCircle(sketch, "E349.MirrorC", {"center": v(-0.9, -3.8) * mm, "radius": 0.1 * mm});
            skCircle(sketch, "E350.MirrorC", {"center": v(-7.9, -3.8) * mm, "radius": 0.1 * mm});
            skCircle(sketch, "E351.MirrorC", {"center": v(-14.9, -3.8) * mm, "radius": 0.1 * mm});
            skCircle(sketch, "E352.MirrorC", {"center": v(-9.9, -3.8) * mm, "radius": 0.1 * mm});
            skCircle(sketch, "E353.MirrorC", {"center": v(-18.9, -3.8) * mm, "radius": 0.1 * mm});
            skCircle(sketch, "E354.MirrorC", {"center": v(-12.9, -3.8) * mm, "radius": 0.1 * mm});
            skCircle(sketch, "E355.MirrorC", {"center": v(-17.9, -3.8) * mm, "radius": 0.1 * mm});
            skCircle(sketch, "E356.MirrorC", {"center": v(-5.9, -3.8) * mm, "radius": 0.1 * mm});
            skCircle(sketch, "E357.MirrorC", {"center": v(-3.9, -3.8) * mm, "radius": 0.1 * mm});
            skCircle(sketch, "E358.MirrorC", {"center": v(-8.9, -3.8) * mm, "radius": 0.1 * mm});
            skCircle(sketch, "E359.MirrorC", {"center": v(-16.9, -3.8) * mm, "radius": 0.1 * mm});
            skCircle(sketch, "E360.MirrorC", {"center": v(-10.9, -3.8) * mm, "radius": 0.1 * mm});
            skCircle(sketch, "E361.MirrorC", {"center": v(-11.9, -3.8) * mm, "radius": 0.1 * mm});
            skCircle(sketch, "E362.MirrorC", {"center": v(-15.9, -3.8) * mm, "radius": 0.1 * mm});
            skCircle(sketch, "E363.MirrorC", {"center": v(-4.9, -3.8) * mm, "radius": 0.1 * mm});
            skCircle(sketch, "E364.MirrorC", {"center": v(-13.9, -3.8) * mm, "radius": 0.1 * mm});
            skCircle(sketch, "E365.MirrorC", {"center": v(-2.9, -3.8) * mm, "radius": 0.1 * mm});
            skCircle(sketch, "E366.MirrorC", {"center": v(-11.9, -2.8) * mm, "radius": 0.1 * mm});
            skCircle(sketch, "E367.MirrorC", {"center": v(-17.9, -2.8) * mm, "radius": 0.1 * mm});
            skCircle(sketch, "E368.MirrorC", {"center": v(-1.9, -2.8) * mm, "radius": 0.1 * mm});
            skCircle(sketch, "E369.MirrorC", {"center": v(-8.9, -2.8) * mm, "radius": 0.1 * mm});
            skCircle(sketch, "E370.MirrorC", {"center": v(-9.9, -2.8) * mm, "radius": 0.1 * mm});
            skCircle(sketch, "E371.MirrorC", {"center": v(-13.9, -2.8) * mm, "radius": 0.1 * mm});
            skCircle(sketch, "E372.MirrorC", {"center": v(-6.9, -2.8) * mm, "radius": 0.1 * mm});
            skCircle(sketch, "E373.MirrorC", {"center": v(-15.9, -2.8) * mm, "radius": 0.1 * mm});
            skCircle(sketch, "E374.MirrorC", {"center": v(-14.9, -2.8) * mm, "radius": 0.1 * mm});
            skCircle(sketch, "E375.MirrorC", {"center": v(-0.9, -2.8) * mm, "radius": 0.1 * mm});
            skCircle(sketch, "E376.MirrorC", {"center": v(-4.9, -2.8) * mm, "radius": 0.1 * mm});
            skCircle(sketch, "E377.MirrorC", {"center": v(-5.9, -2.8) * mm, "radius": 0.1 * mm});
            skCircle(sketch, "E378.MirrorC", {"center": v(-16.9, -2.8) * mm, "radius": 0.1 * mm});
            skCircle(sketch, "E379.MirrorC", {"center": v(-12.9, -2.8) * mm, "radius": 0.1 * mm});
            skCircle(sketch, "E380.MirrorC", {"center": v(-10.9, -2.8) * mm, "radius": 0.1 * mm});
            skCircle(sketch, "E381.MirrorC", {"center": v(-3.9, -2.8) * mm, "radius": 0.1 * mm});
            skCircle(sketch, "E382.MirrorC", {"center": v(-7.9, -2.8) * mm, "radius": 0.1 * mm});
            skCircle(sketch, "E383.MirrorC", {"center": v(-18.9, -2.8) * mm, "radius": 0.1 * mm});
            skCircle(sketch, "E384.MirrorC", {"center": v(-2.9, -2.8) * mm, "radius": 0.1 * mm});
            skCircle(sketch, "E385.MirrorC", {"center": v(-1.9, -1.8) * mm, "radius": 0.1 * mm});
            skCircle(sketch, "E386.MirrorC", {"center": v(-10.9, -1.8) * mm, "radius": 0.1 * mm});
            skCircle(sketch, "E387.MirrorC", {"center": v(-6.9, -1.8) * mm, "radius": 0.1 * mm});
            skCircle(sketch, "E388.MirrorC", {"center": v(-15.9, -1.8) * mm, "radius": 0.1 * mm});
            skCircle(sketch, "E389.MirrorC", {"center": v(-18.9, -1.8) * mm, "radius": 0.1 * mm});
            skCircle(sketch, "E390.MirrorC", {"center": v(-9.9, -1.8) * mm, "radius": 0.1 * mm});
            skCircle(sketch, "E391.MirrorC", {"center": v(-13.9, -1.8) * mm, "radius": 0.1 * mm});
            skCircle(sketch, "E392.MirrorC", {"center": v(-0.9, -1.8) * mm, "radius": 0.1 * mm});
            skCircle(sketch, "E393.MirrorC", {"center": v(-14.9, -1.8) * mm, "radius": 0.1 * mm});
            skCircle(sketch, "E394.MirrorC", {"center": v(-4.9, -1.8) * mm, "radius": 0.1 * mm});
            skCircle(sketch, "E395.MirrorC", {"center": v(-17.9, -1.8) * mm, "radius": 0.1 * mm});
            skCircle(sketch, "E396.MirrorC", {"center": v(-2.9, -1.8) * mm, "radius": 0.1 * mm});
            skCircle(sketch, "E397.MirrorC", {"center": v(-8.9, -1.8) * mm, "radius": 0.1 * mm});
            skCircle(sketch, "E398.MirrorC", {"center": v(-3.9, -1.8) * mm, "radius": 0.1 * mm});
            skCircle(sketch, "E399.MirrorC", {"center": v(-7.9, -1.8) * mm, "radius": 0.1 * mm});
            skCircle(sketch, "E400.MirrorC", {"center": v(-11.9, -1.8) * mm, "radius": 0.1 * mm});
            skCircle(sketch, "E401.MirrorC", {"center": v(-5.9, -1.8) * mm, "radius": 0.1 * mm});
            skCircle(sketch, "E402.MirrorC", {"center": v(-12.9, -1.8) * mm, "radius": 0.1 * mm});
            skCircle(sketch, "E403.MirrorC", {"center": v(-16.9, -1.8) * mm, "radius": 0.1 * mm});
            skCircle(sketch, "E404.MirrorC", {"center": v(-3.9, -0.8) * mm, "radius": 0.1 * mm});
            skCircle(sketch, "E405.MirrorC", {"center": v(-13.9, -0.8) * mm, "radius": 0.1 * mm});
            skCircle(sketch, "E406.MirrorC", {"center": v(-17.9, -0.8) * mm, "radius": 0.1 * mm});
            skCircle(sketch, "E407.MirrorC", {"center": v(-1.9, -0.8) * mm, "radius": 0.1 * mm});
            skCircle(sketch, "E408.MirrorC", {"center": v(-0.9, -0.8) * mm, "radius": 0.1 * mm});
            skCircle(sketch, "E409.MirrorC", {"center": v(-6.9, -0.8) * mm, "radius": 0.1 * mm});
            skCircle(sketch, "E410.MirrorC", {"center": v(-12.9, -0.8) * mm, "radius": 0.1 * mm});
            skCircle(sketch, "E411.MirrorC", {"center": v(-8.9, -0.8) * mm, "radius": 0.1 * mm});
            skCircle(sketch, "E412.MirrorC", {"center": v(-18.9, -0.8) * mm, "radius": 0.1 * mm});
            skCircle(sketch, "E413.MirrorC", {"center": v(-16.9, -0.8) * mm, "radius": 0.1 * mm});
            skCircle(sketch, "E414.MirrorC", {"center": v(-2.9, -0.8) * mm, "radius": 0.1 * mm});
            skCircle(sketch, "E415.MirrorC", {"center": v(-11.9, -0.8) * mm, "radius": 0.1 * mm});
            skCircle(sketch, "E416.MirrorC", {"center": v(-10.9, -0.8) * mm, "radius": 0.1 * mm});
            skCircle(sketch, "E417.MirrorC", {"center": v(-4.9, -0.8) * mm, "radius": 0.1 * mm});
            skCircle(sketch, "E418.MirrorC", {"center": v(-5.9, -0.8) * mm, "radius": 0.1 * mm});
            skCircle(sketch, "E419.MirrorC", {"center": v(-15.9, -0.8) * mm, "radius": 0.1 * mm});
            skCircle(sketch, "E420.MirrorC", {"center": v(-14.9, -0.8) * mm, "radius": 0.1 * mm});
            skCircle(sketch, "E421.MirrorC", {"center": v(-9.9, -0.8) * mm, "radius": 0.1 * mm});
            skCircle(sketch, "E422.MirrorC", {"center": v(-7.9, -0.8) * mm, "radius": 0.1 * mm});
            skSolve(sketch);
        }
        {
            var Q0;
            Q0 = qSketchRegion(id + "F2", true);
            extrude(context, id + "F3", {"entities" : qUnion([Q0]), "oppositeDirection" : true, "depth" : 15 * mm, "offsetDistance" : 25 * mm});
        }
    });
